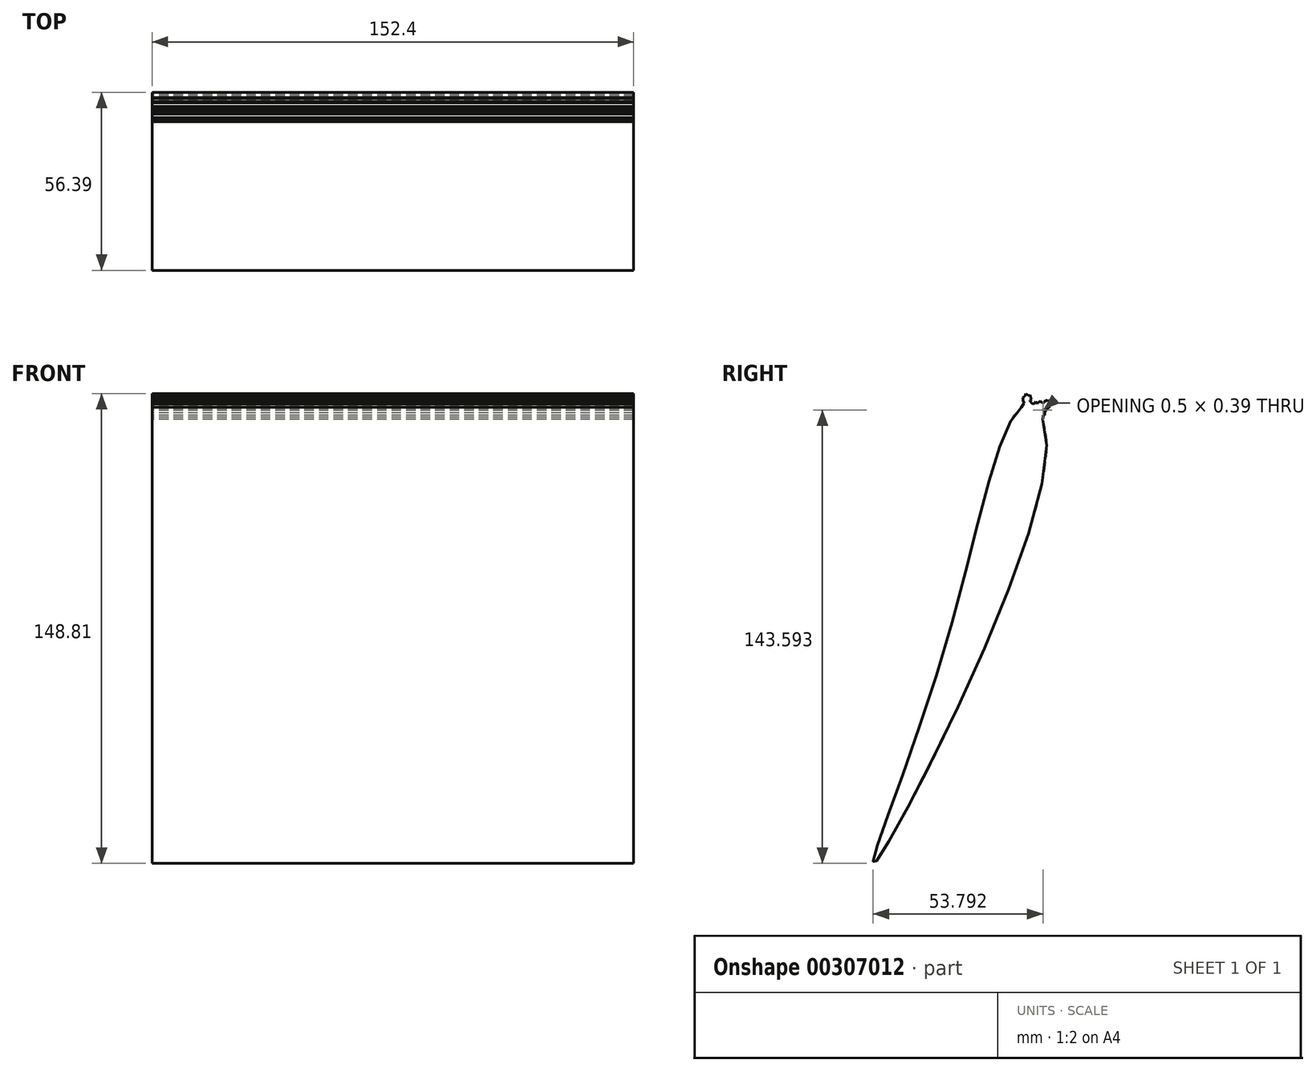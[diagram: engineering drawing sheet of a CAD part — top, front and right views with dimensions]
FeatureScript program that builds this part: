
annotation { "Feature Type Name" : "Feature", "Feature Type Description" : "" }
export const myFeature = defineFeature(function(context is Context, id is Id, definition is map)
    precondition{}
    {
        {
            var Q0;
            Q0=qCreatedBy(makeId("Right.planeOp"),FACE);
            var sketch = newSketch(context, id + "F0", { "sketchPlane" : qUnion([Q0])});
            skFitSpline(sketch, "E0", {"points": [v(44.88, 67.9) * mm, v(52.06, 51.86) * mm, v(-2.03, -76.46) * mm, v(18.89, -12.08) * mm, v(44.88, 67.9) * mm]});
            skLineSegment(sketch, "E1", {"start": v(48.9, 67) * mm, "end": v(51.89, 69.03) * mm});
            skLineSegment(sketch, "E2", {"start": v(51.89, 69.03) * mm, "end": v(52.68, 68.01) * mm});
            skLineSegment(sketch, "E3", {"start": v(52.68, 68.01) * mm, "end": v(49.86, 65.8) * mm});
            skLineSegment(sketch, "E4", {"start": v(49.86, 65.8) * mm, "end": v(48.9, 67) * mm});
            skLineSegment(sketch, "E5", {"start": v(51.89, 69.03) * mm, "end": v(52.64, 69.62) * mm});
            skPoint(sketch, "E5.endSnap0", {"position": v(52.29, 68.52) * mm});
            skLineSegment(sketch, "E6", {"start": v(52.64, 69.62) * mm, "end": v(53.37, 68.55) * mm});
            skLineSegment(sketch, "E7", {"start": v(53.37, 68.55) * mm, "end": v(52.68, 68.01) * mm});
            skLineSegment(sketch, "E8", {"start": v(46.66, 68.17) * mm, "end": v(46.44, 70.8) * mm});
            skLineSegment(sketch, "E9", {"start": v(46.44, 70.8) * mm, "end": v(45.15, 70.7) * mm});
            skLineSegment(sketch, "E10", {"start": v(45.15, 70.7) * mm, "end": v(45.37, 68.08) * mm});
            skLineSegment(sketch, "E11", {"start": v(45.37, 68.08) * mm, "end": v(46.66, 68.17) * mm});
            skLineSegment(sketch, "E12", {"start": v(50.33, 65.16) * mm, "end": v(50.77, 66.52) * mm});
            skLineSegment(sketch, "E13", {"start": v(50.77, 66.52) * mm, "end": v(51.27, 66.9) * mm});
            skLineSegment(sketch, "E14", {"start": v(51.27, 66.9) * mm, "end": v(51.2, 66.66) * mm});
            skPoint(sketch, "E14.endSnap0", {"position": v(51.02, 66.71) * mm});
            skLineSegment(sketch, "E15", {"start": v(51.2, 66.66) * mm, "end": v(50.77, 66.52) * mm});
            skLineSegment(sketch, "E16", {"start": v(50.55, 65.84) * mm, "end": v(51.36, 66.47) * mm});
            skLineSegment(sketch, "E17", {"start": v(51.36, 66.47) * mm, "end": v(51.58, 67.15) * mm});
            skLineSegment(sketch, "E18", {"start": v(51.58, 67.15) * mm, "end": v(51.92, 66.7) * mm});
            skLineSegment(sketch, "E19", {"start": v(51.92, 66.7) * mm, "end": v(51.36, 66.47) * mm});
            skLineSegment(sketch, "E20", {"start": v(52.3, 67.7) * mm, "end": v(53.1, 67.44) * mm});
            skLineSegment(sketch, "E21", {"start": v(53.1, 67.44) * mm, "end": v(52.68, 68.01) * mm});
            skLineSegment(sketch, "E22", {"start": v(53.37, 68.55) * mm, "end": v(53.23, 67.84) * mm});
            skLineSegment(sketch, "E23", {"start": v(53.23, 67.84) * mm, "end": v(52.42, 67.2) * mm});
            skLineSegment(sketch, "E24", {"start": v(52.42, 67.2) * mm, "end": v(51.58, 67.15) * mm});
            skLineSegment(sketch, "E25", {"start": v(52.42, 67.2) * mm, "end": v(52.32, 66.9) * mm});
            skLineSegment(sketch, "E26", {"start": v(52.32, 66.9) * mm, "end": v(51.92, 66.7) * mm});
            skLineSegment(sketch, "E27", {"start": v(53.23, 67.84) * mm, "end": v(52.68, 68.01) * mm});
            skLineSegment(sketch, "E28", {"start": v(51.92, 66.7) * mm, "end": v(51.62, 65.77) * mm});
            skLineSegment(sketch, "E29", {"start": v(51.62, 65.77) * mm, "end": v(50.55, 65.84) * mm});
            skLineSegment(sketch, "E30", {"start": v(53.37, 68.55) * mm, "end": v(53.62, 69.3) * mm});
            skLineSegment(sketch, "E31", {"start": v(53.62, 69.3) * mm, "end": v(53.12, 68.92) * mm});
            skLineSegment(sketch, "E32", {"start": v(53.12, 68.92) * mm, "end": v(53.62, 69.3) * mm});
            skLineSegment(sketch, "E33", {"start": v(53.62, 69.3) * mm, "end": v(52.64, 69.62) * mm});
            skLineSegment(sketch, "E34", {"start": v(52.64, 69.62) * mm, "end": v(51.86, 69.87) * mm});
            skLineSegment(sketch, "E35", {"start": v(51.86, 69.87) * mm, "end": v(51.62, 69.12) * mm});
            skLineSegment(sketch, "E36", {"start": v(51.62, 69.12) * mm, "end": v(50.6, 69.07) * mm});
            skLineSegment(sketch, "E37", {"start": v(50.6, 69.07) * mm, "end": v(50.21, 69.58) * mm});
            skLineSegment(sketch, "E38", {"start": v(50.21, 69.58) * mm, "end": v(49.86, 68.5) * mm});
            skLineSegment(sketch, "E39", {"start": v(49.86, 68.5) * mm, "end": v(49.73, 68.08) * mm});
            skLineSegment(sketch, "E40", {"start": v(49.73, 68.08) * mm, "end": v(48.99, 68.14) * mm});
            skLineSegment(sketch, "E41", {"start": v(48.99, 68.14) * mm, "end": v(48.71, 67.29) * mm});
            skLineSegment(sketch, "E42", {"start": v(48.71, 67.29) * mm, "end": v(48.9, 67) * mm});
            skLineSegment(sketch, "E43", {"start": v(50.21, 69.58) * mm, "end": v(49.13, 68.73) * mm});
            skLineSegment(sketch, "E44", {"start": v(49.13, 68.73) * mm, "end": v(48.68, 69.31) * mm});
            skLineSegment(sketch, "E45", {"start": v(48.68, 69.31) * mm, "end": v(48.2, 68.59) * mm});
            skLineSegment(sketch, "E46", {"start": v(48.2, 68.59) * mm, "end": v(47.5, 68.8) * mm});
            skLineSegment(sketch, "E47", {"start": v(47.5, 68.8) * mm, "end": v(46.87, 68.3) * mm});
            skLineSegment(sketch, "E48", {"start": v(47.5, 68.8) * mm, "end": v(47.03, 69.42) * mm});
            skLineSegment(sketch, "E49", {"start": v(47.03, 69.42) * mm, "end": v(46.62, 69.1) * mm});
            skLineSegment(sketch, "E50", {"start": v(46.62, 69.1) * mm, "end": v(46.88, 69.9) * mm});
            skLineSegment(sketch, "E51", {"start": v(46.88, 69.9) * mm, "end": v(46.48, 70.4) * mm});
            skLineSegment(sketch, "E52", {"start": v(46.48, 70.4) * mm, "end": v(46.44, 70.8) * mm});
            skLineSegment(sketch, "E53", {"start": v(46.88, 69.9) * mm, "end": v(47.1, 70.58) * mm});
            skLineSegment(sketch, "E54", {"start": v(47.1, 70.58) * mm, "end": v(46.48, 70.4) * mm});
            skLineSegment(sketch, "E55", {"start": v(47.1, 70.58) * mm, "end": v(47.5, 70.08) * mm});
            skLineSegment(sketch, "E56", {"start": v(47.5, 70.08) * mm, "end": v(46.88, 69.9) * mm});
            skLineSegment(sketch, "E57", {"start": v(47.1, 70.58) * mm, "end": v(47.03, 71.44) * mm});
            skLineSegment(sketch, "E58", {"start": v(47.03, 71.44) * mm, "end": v(46.44, 70.8) * mm});
            skLineSegment(sketch, "E59", {"start": v(46.44, 70.8) * mm, "end": v(46, 71.37) * mm});
            skPoint(sketch, "E59.endSnap0", {"position": v(45.8, 70.75) * mm});
            skLineSegment(sketch, "E60", {"start": v(46, 71.37) * mm, "end": v(45.15, 70.7) * mm});
            skLineSegment(sketch, "E61", {"start": v(45.15, 70.7) * mm, "end": v(45.55, 71.93) * mm});
            skLineSegment(sketch, "E62", {"start": v(45.55, 71.93) * mm, "end": v(46.74, 71.12) * mm});
            skLineSegment(sketch, "E63", {"start": v(46.74, 71.12) * mm, "end": v(47.03, 71.44) * mm});
            skLineSegment(sketch, "E64", {"start": v(45.3, 71.17) * mm, "end": v(44.61, 70.63) * mm});
            skLineSegment(sketch, "E65", {"start": v(44.61, 70.63) * mm, "end": v(45.29, 69.2) * mm});
            skLineSegment(sketch, "E66", {"start": v(45.29, 69.2) * mm, "end": v(44.72, 69.71) * mm});
            skLineSegment(sketch, "E67", {"start": v(44.72, 69.71) * mm, "end": v(44.68, 70.18) * mm});
            skLineSegment(sketch, "E68", {"start": v(44.68, 70.18) * mm, "end": v(44.61, 70.63) * mm});
            skLineSegment(sketch, "E69", {"start": v(45.37, 68.08) * mm, "end": v(44.88, 67.9) * mm});
            skLineSegment(sketch, "E70", {"start": v(44.88, 67.9) * mm, "end": v(44.82, 68.6) * mm});
            skLineSegment(sketch, "E71", {"start": v(44.82, 68.6) * mm, "end": v(45.34, 69.09) * mm});
            skLineSegment(sketch, "E72", {"start": v(45.34, 69.09) * mm, "end": v(44.72, 69.71) * mm});
            skLineSegment(sketch, "E73", {"start": v(44.72, 69.71) * mm, "end": v(45.08, 68.84) * mm});
            skLineSegment(sketch, "E74", {"start": v(51.62, 65.77) * mm, "end": v(51.58, 65.07) * mm});
            skLineSegment(sketch, "E75", {"start": v(51.58, 65.07) * mm, "end": v(51.05, 65.05) * mm});
            skLineSegment(sketch, "E76", {"start": v(51.05, 65.05) * mm, "end": v(51.09, 64.41) * mm});
            skLineSegment(sketch, "E77", {"start": v(51.09, 64.41) * mm, "end": v(50.88, 63.78) * mm});
            skLineSegment(sketch, "E78", {"start": v(50.88, 63.78) * mm, "end": v(50.33, 65.16) * mm});
            skLineSegment(sketch, "E79", {"start": v(44.82, 68.6) * mm, "end": v(44.24, 67.56) * mm});
            skLineSegment(sketch, "E80", {"start": v(44.24, 67.56) * mm, "end": v(44.88, 67.9) * mm});
            skLineSegment(sketch, "E81", {"start": v(46.88, 69.9) * mm, "end": v(47.03, 69.42) * mm});
            skLineSegment(sketch, "E82.0", {"start": v(44.82, 68.6) * mm, "end": v(51.36, 66.47) * mm, "construction": true});
            skLineSegment(sketch, "E83.0", {"start": v(44.68, 70.18) * mm, "end": v(53.1, 67.44) * mm, "construction": true});
            skLineSegment(sketch, "E84.0", {"start": v(44.72, 69.71) * mm, "end": v(47.5, 68.8) * mm, "construction": true});
            skLineSegment(sketch, "E85.0", {"start": v(45.29, 69.2) * mm, "end": v(52.32, 66.9) * mm, "construction": true});
            skLineSegment(sketch, "E86.0", {"start": v(44.61, 70.63) * mm, "end": v(53.23, 67.84) * mm, "construction": true});
            skLineSegment(sketch, "E87.0", {"start": v(45.55, 71.93) * mm, "end": v(53.62, 69.3) * mm, "construction": true});
            skLineSegment(sketch, "E88.0", {"start": v(45.3, 71.17) * mm, "end": v(53.37, 68.55) * mm, "construction": true});
            skLineSegment(sketch, "E89.0", {"start": v(46.48, 70.4) * mm, "end": v(52.29, 68.52) * mm, "construction": true});
            skLineSegment(sketch, "E90.0", {"start": v(51.02, 66.71) * mm, "end": v(51.2, 66.66) * mm, "construction": true});
            skLineSegment(sketch, "E91.0", {"start": v(49.13, 68.73) * mm, "end": v(49.86, 68.5) * mm, "construction": true});
            skLineSegment(sketch, "E92.0", {"start": v(49.73, 68.08) * mm, "end": v(52.42, 67.2) * mm, "construction": true});
            skLineSegment(sketch, "E93.0", {"start": v(45.29, 69.2) * mm, "end": v(46, 71.37) * mm, "construction": true});
            skLineSegment(sketch, "E94.0", {"start": v(52.42, 67.2) * mm, "end": v(52.68, 68.01) * mm, "construction": true});
            skLineSegment(sketch, "E95.0", {"start": v(45.15, 70.7) * mm, "end": v(45.3, 71.17) * mm, "construction": true});
            skLineSegment(sketch, "E96.0", {"start": v(52.29, 68.52) * mm, "end": v(52.64, 69.62) * mm, "construction": true});
            skLineSegment(sketch, "E97.0", {"start": v(50.55, 65.84) * mm, "end": v(51.86, 69.87) * mm, "construction": true});
            skLineSegment(sketch, "E98.0", {"start": v(53.1, 67.44) * mm, "end": v(53.23, 67.84) * mm, "construction": true});
            skSolve(sketch);
        }
        {
            var Q0;
            Q0=qSketchRegion(id+"F0",true);
            var Q1;
            Q1=makeQuery(id+"F0.imprint","IMPRINT",FACE,{"disambiguationData":[TD([[makeQuery(id+"F0.imprint","IMPRINT",EDGE,{"derivedFrom":sQuery(id+"F0.wireOp",EDGE,"E1")}),1.0]])]});
            var Q2;
            {var subQ3=sQuery(id+"F0.wireOp",EDGE,"E1");Q2=makeQuery(id+"F0.imprint","IMPRINT",FACE,{"disambiguationData":[TD([[makeQuery(id+"F0.imprint","IMPRINT",EDGE,{"derivedFrom":subQ3}),-1.0]])]});}
            var Q3;
            {var subQ0=sQuery(id+"F0.wireOp",EDGE,"E29");Q3=makeQuery(id+"F0.imprint","IMPRINT",FACE,{"disambiguationData":[TD([[makeQuery(id+"F0.imprint","IMPRINT",EDGE,{"derivedFrom":subQ0}),1.0]])]});}
            var Q4;
            {var subQ0=sQuery(id+"F0.wireOp",EDGE,"E78");var subQ1=sQuery(id+"F0.wireOp",EDGE,"E12");var subQ2=makeQuery(id+"F0.imprint","INTERSECT",VERTEX,{"derivedFrom":[subQ1,subQ0]});Q4=makeQuery(id+"F0.imprint","IMPRINT",FACE,{"disambiguationData":[TD([[makeQuery(id+"F0.imprint","IMPRINT",EDGE,{"disambiguationData":[TD([[subQ2,1.0]])],"derivedFrom":subQ0}),1.0]])]});}
            var Q5;
            {var subQ2=sQuery(id+"F0.wireOp",EDGE,"E8");Q5=makeQuery(id+"F0.imprint","IMPRINT",FACE,{"disambiguationData":[TD([[makeQuery(id+"F0.imprint","IMPRINT",EDGE,{"derivedFrom":subQ2}),-1.0]])]});}
            var Q6;
            {var subQ0=sQuery(id+"F0.wireOp",EDGE,"E11");Q6=makeQuery(id+"F0.imprint","IMPRINT",FACE,{"disambiguationData":[TD([[makeQuery(id+"F0.imprint","IMPRINT",EDGE,{"derivedFrom":subQ0}),1.0]])]});}
            var Q7;
            {var subQ0=sQuery(id+"F0.wireOp",EDGE,"E4");Q7=makeQuery(id+"F0.imprint","IMPRINT",FACE,{"disambiguationData":[TD([[makeQuery(id+"F0.imprint","IMPRINT",EDGE,{"derivedFrom":subQ0}),-1.0]])]});}
            var Q8;
            {var subQ0=sQuery(id+"F0.wireOp",EDGE,"E78");var subQ1=sQuery(id+"F0.wireOp",EDGE,"E0");var subQ3=makeQuery(id+"F0.imprint","INTERSECT",VERTEX,{"derivedFrom":[subQ1,subQ0]});Q8=makeQuery(id+"F0.imprint","IMPRINT",FACE,{"disambiguationData":[TD([[makeQuery(id+"F0.imprint","IMPRINT",EDGE,{"disambiguationData":[TD([[subQ3,-1.0]])],"derivedFrom":subQ1}),-1.0]])]});}
            var Q9;
            {var subQ6=sQuery(id+"F0.wireOp",EDGE,"E8");Q9=makeQuery(id+"F0.imprint","IMPRINT",FACE,{"disambiguationData":[TD([[makeQuery(id+"F0.imprint","IMPRINT",EDGE,{"derivedFrom":subQ6}),1.0]])]});}
            var Q10;
            Q10=makeQuery(id+"F0.imprint","IMPRINT",FACE,{"disambiguationData":[TD([[makeQuery(id+"F0.imprint","IMPRINT",EDGE,{"derivedFrom":sQuery(id+"F0.wireOp",EDGE,"E58")}),-1.0]])]});
            var Q11;
            {var subQ0=sQuery(id+"F0.wireOp",EDGE,"E69");Q11=makeQuery(id+"F0.imprint","IMPRINT",FACE,{"disambiguationData":[TD([[makeQuery(id+"F0.imprint","IMPRINT",EDGE,{"derivedFrom":subQ0}),-1.0]])]});}
            var Q12;
            {var subQ1=sQuery(id+"F0.wireOp",EDGE,"E70");Q12=makeQuery(id+"F0.imprint","IMPRINT",FACE,{"disambiguationData":[TD([[makeQuery(id+"F0.imprint","IMPRINT",EDGE,{"derivedFrom":subQ1}),1.0]])]});}
            var Q13;
            {var subQ0=sQuery(id+"F0.wireOp",EDGE,"E80");Q13=makeQuery(id+"F0.imprint","IMPRINT",FACE,{"disambiguationData":[TD([[makeQuery(id+"F0.imprint","IMPRINT",EDGE,{"derivedFrom":subQ0}),1.0]])]});}
            var Q14;
            {var subQ5=sQuery(id+"F0.wireOp",EDGE,"E64");Q14=makeQuery(id+"F0.imprint","IMPRINT",FACE,{"disambiguationData":[TD([[makeQuery(id+"F0.imprint","IMPRINT",EDGE,{"derivedFrom":subQ5}),1.0]])]});}
            var Q15;
            {var subQ1=sQuery(id+"F0.wireOp",EDGE,"E70");Q15=makeQuery(id+"F0.imprint","IMPRINT",FACE,{"disambiguationData":[TD([[makeQuery(id+"F0.imprint","IMPRINT",EDGE,{"derivedFrom":subQ1}),-1.0]])]});}
            var Q16;
            {var subQ0=sQuery(id+"F0.wireOp",EDGE,"E67");Q16=makeQuery(id+"F0.imprint","IMPRINT",FACE,{"disambiguationData":[TD([[makeQuery(id+"F0.imprint","IMPRINT",EDGE,{"derivedFrom":subQ0}),-1.0]])]});}
            var Q17;
            {var subQ0=sQuery(id+"F0.wireOp",EDGE,"E72");var subQ1=sQuery(id+"F0.wireOp",EDGE,"E10");var subQ2=makeQuery(id+"F0.imprint","INTERSECT",VERTEX,{"derivedFrom":[subQ1,subQ0]});Q17=makeQuery(id+"F0.imprint","IMPRINT",FACE,{"disambiguationData":[TD([[makeQuery(id+"F0.imprint","IMPRINT",EDGE,{"disambiguationData":[TD([[subQ2,-1.0]])],"derivedFrom":subQ1}),1.0]])]});}
            var Q18;
            Q18=makeQuery(id+"F0.imprint","IMPRINT",FACE,{"disambiguationData":[TD([[makeQuery(id+"F0.imprint","IMPRINT",EDGE,{"derivedFrom":sQuery(id+"F0.wireOp",EDGE,"E9")}),-1.0]])]});
            var Q19;
            Q19=makeQuery(id+"F0.imprint","IMPRINT",FACE,{"disambiguationData":[TD([[makeQuery(id+"F0.imprint","IMPRINT",EDGE,{"derivedFrom":sQuery(id+"F0.wireOp",EDGE,"E17")}),-1.0]])]});
            var Q20;
            {var subQ0=sQuery(id+"F0.wireOp",EDGE,"E65");var subQ1=sQuery(id+"F0.wireOp",EDGE,"E10");var subQ2=makeQuery(id+"F0.imprint","INTERSECT",VERTEX,{"derivedFrom":[subQ1,subQ0]});Q20=makeQuery(id+"F0.imprint","IMPRINT",FACE,{"disambiguationData":[TD([[makeQuery(id+"F0.imprint","IMPRINT",EDGE,{"disambiguationData":[TD([[subQ2,-1.0]])],"derivedFrom":subQ1}),1.0]])]});}
            var Q21;
            Q21=makeQuery(id+"F0.imprint","IMPRINT",FACE,{"disambiguationData":[TD([[makeQuery(id+"F0.imprint","IMPRINT",EDGE,{"derivedFrom":sQuery(id+"F0.wireOp",EDGE,"E18")}),1.0]])]});
            var Q22;
            Q22=makeQuery(id+"F0.imprint","IMPRINT",FACE,{"disambiguationData":[TD([[makeQuery(id+"F0.imprint","IMPRINT",EDGE,{"derivedFrom":sQuery(id+"F0.wireOp",EDGE,"E49")}),-1.0]])]});
            var Q23;
            {var subQ2=sQuery(id+"F0.wireOp",EDGE,"E32");Q23=makeQuery(id+"F0.imprint","IMPRINT",FACE,{"disambiguationData":[TD([[makeQuery(id+"F0.imprint","IMPRINT",EDGE,{"derivedFrom":subQ2}),1.0]])]});}
            var Q24;
            {var subQ0=sQuery(id+"F0.wireOp",EDGE,"E66");var subQ1=sQuery(id+"F0.wireOp",EDGE,"E10");var subQ2=makeQuery(id+"F0.imprint","INTERSECT",VERTEX,{"derivedFrom":[subQ1,subQ0]});Q24=makeQuery(id+"F0.imprint","IMPRINT",FACE,{"disambiguationData":[TD([[makeQuery(id+"F0.imprint","IMPRINT",EDGE,{"disambiguationData":[TD([[subQ2,-1.0]])],"derivedFrom":subQ1}),-1.0]])]});}
            var Q25;
            Q25=makeQuery(id+"F0.imprint","IMPRINT",FACE,{"disambiguationData":[TD([[makeQuery(id+"F0.imprint","IMPRINT",EDGE,{"derivedFrom":sQuery(id+"F0.wireOp",EDGE,"E2")}),1.0]])]});
            var Q26;
            {var subQ5=sQuery(id+"F0.wireOp",EDGE,"E73");Q26=makeQuery(id+"F0.imprint","IMPRINT",FACE,{"disambiguationData":[TD([[makeQuery(id+"F0.imprint","IMPRINT",EDGE,{"derivedFrom":subQ5}),1.0]])]});}
            var Q27;
            {var subQ1=sQuery(id+"F0.wireOp",EDGE,"E14");Q27=makeQuery(id+"F0.imprint","IMPRINT",FACE,{"disambiguationData":[TD([[makeQuery(id+"F0.imprint","IMPRINT",EDGE,{"derivedFrom":subQ1}),1.0]])]});}
            var Q28;
            Q28=makeQuery(id+"F0.imprint","IMPRINT",FACE,{"disambiguationData":[TD([[makeQuery(id+"F0.imprint","IMPRINT",EDGE,{"derivedFrom":sQuery(id+"F0.wireOp",EDGE,"E16")}),-1.0]])]});
            var Q29;
            {var subQ0=sQuery(id+"F0.wireOp",EDGE,"E24");Q29=makeQuery(id+"F0.imprint","IMPRINT",FACE,{"disambiguationData":[TD([[makeQuery(id+"F0.imprint","IMPRINT",EDGE,{"derivedFrom":subQ0}),-1.0]])]});}
            var Q30;
            Q30=makeQuery(id+"F0.imprint","IMPRINT",FACE,{"disambiguationData":[TD([[makeQuery(id+"F0.imprint","IMPRINT",EDGE,{"derivedFrom":sQuery(id+"F0.wireOp",EDGE,"E13")}),-1.0]])]});
            var Q31;
            {var subQ0=sQuery(id+"F0.wireOp",EDGE,"E21");var subQ1=sQuery(id+"F0.wireOp",EDGE,"E20");var subQ2=makeQuery(id+"F0.imprint","INTERSECT",VERTEX,{"derivedFrom":[subQ1,subQ0]});Q31=makeQuery(id+"F0.imprint","IMPRINT",FACE,{"disambiguationData":[TD([[makeQuery(id+"F0.imprint","IMPRINT",EDGE,{"disambiguationData":[TD([[subQ2,1.0]])],"derivedFrom":subQ1}),1.0]])]});}
            var Q32;
            Q32=makeQuery(id+"F0.imprint","IMPRINT",FACE,{"disambiguationData":[TD([[makeQuery(id+"F0.imprint","IMPRINT",EDGE,{"derivedFrom":sQuery(id+"F0.wireOp",EDGE,"E53")}),-1.0]])]});
            var Q33;
            {var subQ0=sQuery(id+"F0.wireOp",EDGE,"E30");Q33=makeQuery(id+"F0.imprint","IMPRINT",FACE,{"disambiguationData":[TD([[makeQuery(id+"F0.imprint","IMPRINT",EDGE,{"derivedFrom":subQ0}),1.0]])]});}
            var Q34;
            Q34=makeQuery(id+"F0.imprint","IMPRINT",FACE,{"disambiguationData":[TD([[makeQuery(id+"F0.imprint","IMPRINT",EDGE,{"derivedFrom":sQuery(id+"F0.wireOp",EDGE,"E7")}),1.0]])]});
            var Q35;
            Q35=makeQuery(id+"F0.imprint","IMPRINT",FACE,{"disambiguationData":[TD([[makeQuery(id+"F0.imprint","IMPRINT",EDGE,{"derivedFrom":sQuery(id+"F0.wireOp",EDGE,"E51")}),-1.0]])]});
            var Q36;
            Q36=makeQuery(id+"F0.imprint","IMPRINT",FACE,{"disambiguationData":[TD([[makeQuery(id+"F0.imprint","IMPRINT",EDGE,{"derivedFrom":sQuery(id+"F0.wireOp",EDGE,"E52")}),-1.0]])]});
            var Q37;
            {var subQ1=sQuery(id+"F0.wireOp",EDGE,"E3");var subQ3=sQuery(id+"F0.wireOp",EDGE,"E20");var subQ4=makeQuery(id+"F0.imprint","INTERSECT",VERTEX,{"derivedFrom":[subQ1,subQ3]});Q37=makeQuery(id+"F0.imprint","IMPRINT",FACE,{"disambiguationData":[TD([[makeQuery(id+"F0.imprint","IMPRINT",EDGE,{"disambiguationData":[TD([[subQ4,-1.0]])],"derivedFrom":subQ3}),1.0]])]});}
            var Q38;
            {var subQ0=sQuery(id+"F0.wireOp",EDGE,"E27");Q38=makeQuery(id+"F0.imprint","IMPRINT",FACE,{"disambiguationData":[TD([[makeQuery(id+"F0.imprint","IMPRINT",EDGE,{"derivedFrom":subQ0}),1.0]])]});}
            var Q39;
            {var subQ4=sQuery(id+"F0.wireOp",EDGE,"E4");Q39=makeQuery(id+"F0.imprint","IMPRINT",FACE,{"disambiguationData":[TD([[makeQuery(id+"F0.imprint","IMPRINT",EDGE,{"derivedFrom":subQ4}),1.0]])]});}
            extrude(context, id + "F1", {"entities" : qUnion([Q0, Q1, Q2, Q3, Q4, Q5, Q6, Q7, Q8, Q9, Q10, Q11, Q12, Q13, Q14, Q15, Q16, Q17, Q18, Q19, Q20, Q21, Q22, Q23, Q24, Q25, Q26, Q27, Q28, Q29, Q30, Q31, Q32, Q33, Q34, Q35, Q36, Q37, Q38, Q39]), "depth" : 76.2 * mm, "hasSecondDirection" : true, "secondDirectionOppositeDirection" : true, "secondDirectionDepth" : 76.2 * mm});
        }
    });
